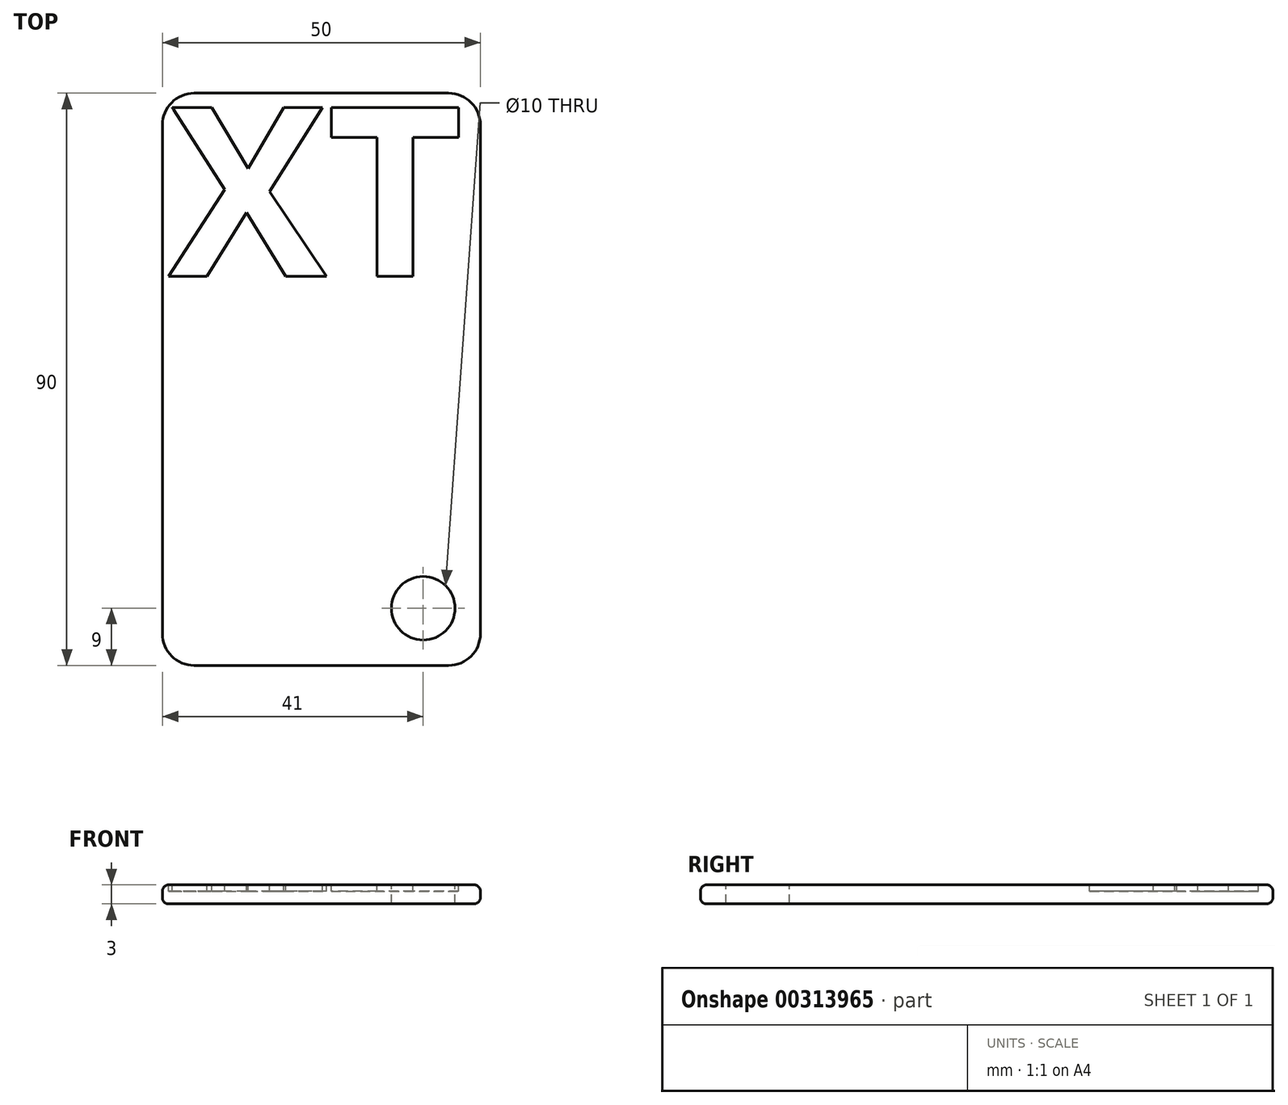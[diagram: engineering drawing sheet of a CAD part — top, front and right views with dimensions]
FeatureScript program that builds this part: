
annotation { "Feature Type Name" : "Feature", "Feature Type Description" : "" }
export const myFeature = defineFeature(function(context is Context, id is Id, definition is map)
    precondition{}
    {
        {
            var Q0;
            Q0=qCreatedBy(makeId("Top.planeOp"),FACE);
            var sketch = newSketch(context, id + "F0", { "sketchPlane" : qUnion([Q0])});
            skLineSegment(sketch, "E0.bottom", {"start": v(-45, 25) * mm, "end": v(45, 25) * mm});
            skLineSegment(sketch, "E0.top", {"start": v(-45, -25) * mm, "end": v(45, -25) * mm});
            skLineSegment(sketch, "E0.left", {"start": v(-45, 25) * mm, "end": v(-45, -25) * mm});
            skLineSegment(sketch, "E0.right", {"start": v(45, 25) * mm, "end": v(45, -25) * mm});
            skLineSegment(sketch, "E1", {"start": v(-45, 25) * mm, "end": v(45, -25) * mm, "construction": true});
            skSolve(sketch);
        }
        {
            var Q0;
            Q0=makeQuery(id+"F0.imprint","IMPRINT",FACE,{"disambiguationData":[TD([[makeQuery(id+"F0.imprint","IMPRINT",EDGE,{"derivedFrom":sQuery(id+"F0.wireOp",EDGE,"E0.bottom")}),-1.0]])]});
            extrude(context, id + "F1", {"entities" : qUnion([Q0]), "depth" : 3 * mm});
        }
        {
            var Q0;
            Q0=makeQuery(id+"F1.opExtrude","CAP_FACE",FACE,{"disambiguationData":[OSD([sQuery(id+"F0.wireOp",EDGE,"E0.bottom"),sQuery(id+"F0.wireOp",EDGE,"E0.top"),sQuery(id+"F0.wireOp",EDGE,"E0.left"),sQuery(id+"F0.wireOp",EDGE,"E0.right")])],"isStart":false});
            var Q1;
            Q1=makeQuery(id+"F1.opExtrude","CAP_FACE",FACE,{"disambiguationData":[OSD([sQuery(id+"F0.wireOp",EDGE,"E0.bottom"),sQuery(id+"F0.wireOp",EDGE,"E0.top"),sQuery(id+"F0.wireOp",EDGE,"E0.left"),sQuery(id+"F0.wireOp",EDGE,"E0.right")])],"isStart":true});
            fillet(context, id + "F2", {"entities" : qUnion([Q0, Q1]), "radius" : 1 * mm, "tangentPropagation" : true, "allowEdgeOverflow" : false});
        }
        {
            var Q0;
            Q0=makeQuery(id+"F1.opExtrude","SWEPT_EDGE",EDGE,{"disambiguationData":[OSD([sQuery(id+"F0.wireOp",EDGE,"E0.top"),sQuery(id+"F0.wireOp",EDGE,"E0.right")])]});
            var Q1;
            Q1=makeQuery(id+"F1.opExtrude","SWEPT_EDGE",EDGE,{"disambiguationData":[OSD([sQuery(id+"F0.wireOp",EDGE,"E0.bottom"),sQuery(id+"F0.wireOp",EDGE,"E0.right")])]});
            var Q2;
            Q2=makeQuery(id+"F1.opExtrude","SWEPT_EDGE",EDGE,{"disambiguationData":[OSD([sQuery(id+"F0.wireOp",EDGE,"E0.bottom"),sQuery(id+"F0.wireOp",EDGE,"E0.left")])]});
            var Q3;
            Q3=makeQuery(id+"F1.opExtrude","SWEPT_EDGE",EDGE,{"disambiguationData":[OSD([sQuery(id+"F0.wireOp",EDGE,"E0.top"),sQuery(id+"F0.wireOp",EDGE,"E0.left")])]});
            fillet(context, id + "F3", {"entities" : qUnion([Q0, Q1, Q2, Q3]), "radius" : 5 * mm, "tangentPropagation" : true, "allowEdgeOverflow" : false});
        }
        {
            var Q0;
            Q0=qCreatedBy(makeId("Right.planeOp"),FACE);
            var sketch = newSketch(context, id + "F4", { "sketchPlane" : qUnion([Q0])});
            skLineSegment(sketch, "E2", {"start": v(0, 0) * mm, "end": v(0, 32.9) * mm});
            skSolve(sketch);
        }
        {
            var Q0;
            Q0=makeQuery(id+"F1.opExtrude","SWEPT_BODY",BODY,{"disambiguationData":[OSD([sQuery(id+"F0.wireOp",EDGE,"E0.bottom"),sQuery(id+"F0.wireOp",EDGE,"E0.top"),sQuery(id+"F0.wireOp",EDGE,"E0.left"),sQuery(id+"F0.wireOp",EDGE,"E0.right")])]});
            var Q1;
            Q1=sQuery(id+"F4.wireOp",EDGE,"E2");
            transform(context, id + "F5", {"entities" : qUnion([Q0]), "transformType" : TransformType.ROTATION, "transformAxis" : qUnion([Q1]), "angle" : 90 * degree, "makeCopy" : false});
        }
        {
            var Q0;
            Q0=makeQuery(id+"F1.opExtrude","CAP_FACE",FACE,{"disambiguationData":[OSD([sQuery(id+"F0.wireOp",EDGE,"E0.bottom"),sQuery(id+"F0.wireOp",EDGE,"E0.top"),sQuery(id+"F0.wireOp",EDGE,"E0.left"),sQuery(id+"F0.wireOp",EDGE,"E0.right")])],"isStart":false});
            var sketch = newSketch(context, id + "F6", { "sketchPlane" : qUnion([Q0])});
            skText(sketch, "E3", { "text": "XT", "fontName": "OpenSans-Bold.ttf"});
            const initialGuessF6  = {"E3": [-0.024, 0.01618, 1, 0, 0.02677]};
            skSetInitialGuess(sketch, initialGuessF6);
            skSolve(sketch);
        }
        {
            var Q0;
            Q0=qSketchRegion(id+"F6",true);
            extrude(context, id + "F7", {"entities" : qUnion([Q0]), "operationType" : NewBodyOperationType.REMOVE, "oppositeDirection" : true, "depth" : 1 * mm});
        }
        {
            var Q0;
            {var subQ0=sQuery(id+"F0.wireOp",EDGE,"E0.left");var subQ2=sQuery(id+"F0.wireOp",EDGE,"E0.bottom");var subQ4=sQuery(id+"F0.wireOp",EDGE,"E0.right");var subQ6=sQuery(id+"F0.wireOp",EDGE,"E0.top");Q0=makeQuery(id+"F7.boolean.opBoolean","SPLIT",FACE,{"disambiguationData":[TD([makeQuery(id+"F7.opExtrude","SWEPT_FACE",FACE,{"disambiguationData":[OSD([sQuery(id+"F6.wireOp",EDGE,"E3.sketch_text.stroke-0")])]})])],"derivedFrom":makeQuery(id+"F1.opExtrude","CAP_FACE",FACE,{"disambiguationData":[OSD([subQ2,subQ6,subQ0,subQ4])],"isStart":false})});}
            var sketch = newSketch(context, id + "F8", { "sketchPlane" : qUnion([Q0])});
            skCircle(sketch, "E4", {"center": v(16, -36) * mm, "radius": 5 * mm});
            skSolve(sketch);
        }
        {
            var Q0;
            Q0=qSketchRegion(id+"F8",true);
            extrude(context, id + "F9", {"entities" : qUnion([Q0]), "operationType" : NewBodyOperationType.REMOVE, "oppositeDirection" : true, "depth" : 3 * mm});
        }
    });
